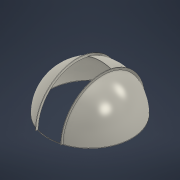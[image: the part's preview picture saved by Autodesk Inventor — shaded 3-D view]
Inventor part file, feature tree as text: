
AUTODESK INVENTOR PART (.ipt)
format: ipt  version: 2022 (Build 260153000, 153)  size: 211,968 bytes
history: native  units: mm
features: revolve x3, sketch x2, extrude x1, plane x1
ambient origin geometry x8: Origin, YZ Plane, XZ Plane, XY Plane, X Axis, Y Axis, Z Axis, Center Point
bodies: Body1 (feature_tree)
feature tree (7):
  extrude  "Extrusion2"  TaperAngle=0.0deg  [1 undecoded]
  plane  "Work Plane3"
  sketch  "Sketch7"  dims[d12=1840.0mm d13=180.0deg d14=105.0deg d15=180.0deg d2=0.5mm d3=0.872665mm d4=0.5mm d5=0.872665mm d7=0.872665mm d8=0.872665mm]
  revolve  "Revolution4"  Angle=180.0deg
  revolve  "Revolution5"  Angle=105.0deg
  revolve  "Revolution6"  Angle=180.0deg
  sketch  "Sketch6"  dims[d9=40.0mm d10=0.0mm d11=0.0mm]
note: 1 required parameter value undecoded (feature->parameter linkage not recoverable at this tier; creation-order binding heuristic only, values carry confidence <= 0.55)
